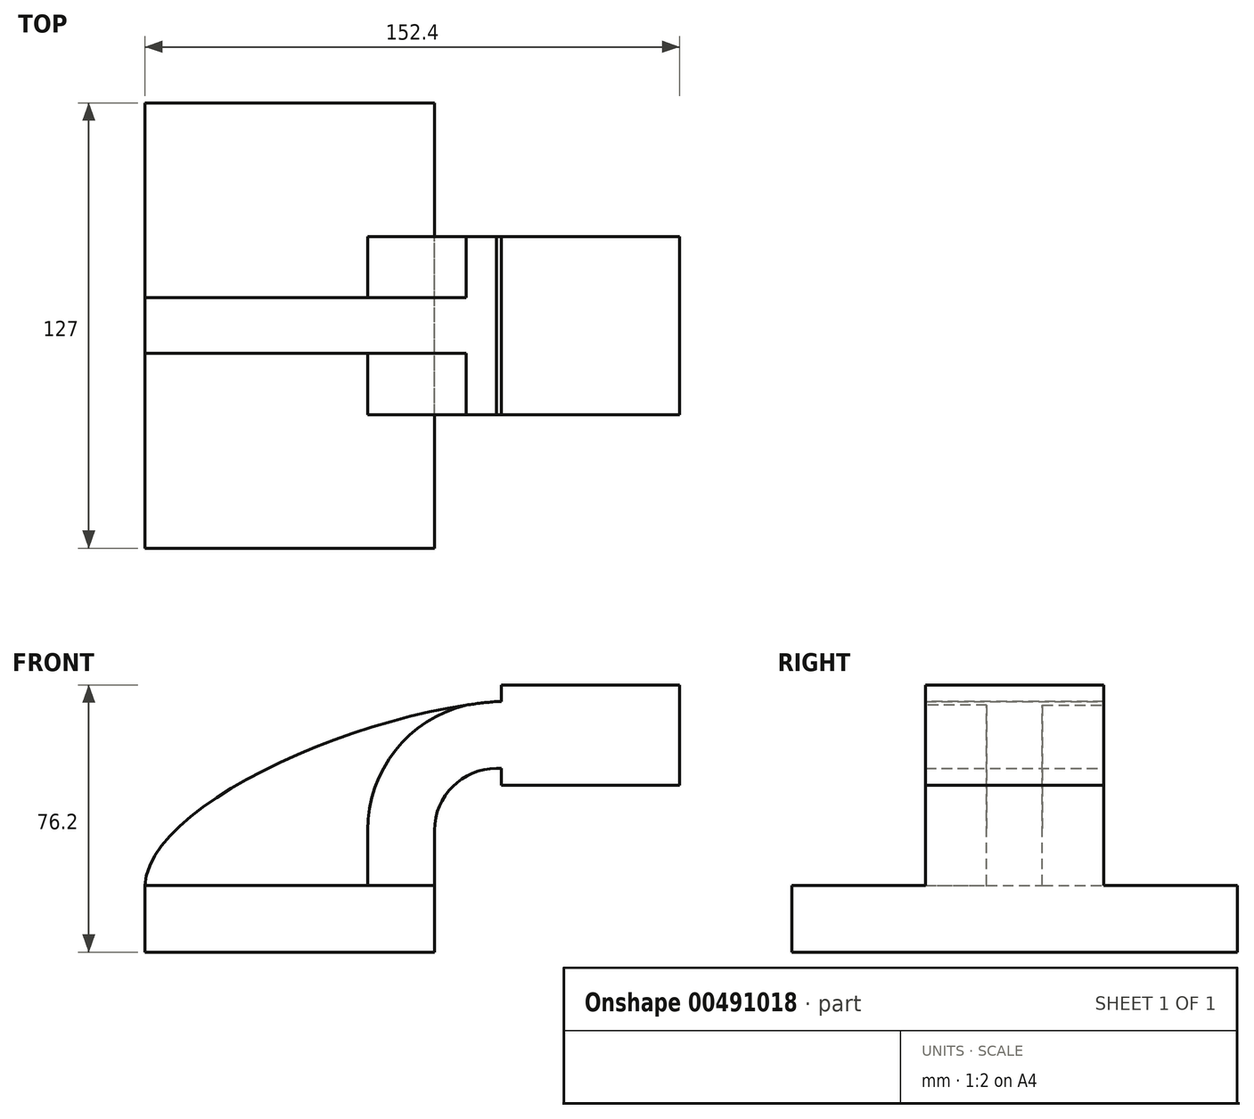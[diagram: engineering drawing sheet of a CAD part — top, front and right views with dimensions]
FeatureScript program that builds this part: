
annotation { "Feature Type Name" : "Feature", "Feature Type Description" : "" }
export const myFeature = defineFeature(function(context is Context, id is Id, definition is map)
    precondition{}
    {
        {
            var Q0;
            Q0=qCreatedBy(makeId("Front.planeOp"),FACE);
            var sketch = newSketch(context, id + "F0", { "sketchPlane" : qUnion([Q0])});
            skLineSegment(sketch, "E0.bottom", {"start": v(-41.28, 9.52) * mm, "end": v(41.27, 9.53) * mm});
            skLineSegment(sketch, "E0.top", {"start": v(-41.28, -9.52) * mm, "end": v(41.28, -9.52) * mm});
            skLineSegment(sketch, "E0.left", {"start": v(-41.28, 9.52) * mm, "end": v(-41.28, -9.53) * mm});
            skLineSegment(sketch, "E0.right", {"start": v(41.27, 9.53) * mm, "end": v(41.28, -9.52) * mm});
            skPoint(sketch, "E0.middle", {"position": v(0, 0) * mm});
            skLineSegment(sketch, "E1.bottom", {"start": v(60.32, 66.68) * mm, "end": v(111.12, 66.68) * mm});
            skLineSegment(sketch, "E1.top", {"start": v(60.32, 38.1) * mm, "end": v(111.12, 38.1) * mm});
            skLineSegment(sketch, "E1.left", {"start": v(60.32, 66.68) * mm, "end": v(60.32, 38.1) * mm});
            skLineSegment(sketch, "E1.right", {"start": v(111.12, 66.68) * mm, "end": v(111.12, 38.1) * mm});
            skPoint(sketch, "E1.middle", {"position": v(85.72, 52.39) * mm});
            skLineSegment(sketch, "E2", {"start": v(41.27, 9.53) * mm, "end": v(41.27, 25.25) * mm});
            skArc(sketch, "E3", {"start": v(41.27, 25.25) * mm, "mid": v(46.44, 37.71) * mm, "end": v(58.9, 42.88) * mm});
            skLineSegment(sketch, "E4", {"start": v(58.9, 42.88) * mm, "end": v(85.72, 42.88) * mm});
            skLineSegment(sketch, "E5.0", {"start": v(58.9, 61.93) * mm, "end": v(85.72, 61.93) * mm});
            skArc(sketch, "E5.1", {"start": v(22.22, 25.25) * mm, "mid": v(32.97, 51.18) * mm, "end": v(58.9, 61.93) * mm});
            skLineSegment(sketch, "E5.2", {"start": v(22.22, 9.53) * mm, "end": v(22.22, 25.25) * mm});
            skLineSegment(sketch, "E6", {"start": v(85.72, 38.1) * mm, "end": v(85.72, 66.68) * mm});
            skFitSpline(sketch, "E7", {"points": [v(-41.28, 9.53) * mm, v(58.9, 61.93) * mm], "startDerivative": vector(3.05, 68.36) * mm, "endDerivative": vector(121.34, 10.24) * mm});
            skSolve(sketch);
        }
        {
            var Q0;
            Q0=makeQuery(id+"F0.imprint","IMPRINT",FACE,{"disambiguationData":[TD([[makeQuery(id+"F0.imprint","IMPRINT",EDGE,{"derivedFrom":sQuery(id+"F0.wireOp",EDGE,"E0.top")}),1.0]])]});
            extrude(context, id + "F1", {"entities" : qUnion([Q0]), "endBound" : BoundingType.SYMMETRIC, "depth" : 127 * mm});
        }
        {
            var Q0;
            {var subQ1=sQuery(id+"F0.wireOp",EDGE,"E2");Q0=makeQuery(id+"F0.imprint","IMPRINT",FACE,{"disambiguationData":[TD([[makeQuery(id+"F0.imprint","IMPRINT",EDGE,{"derivedFrom":subQ1}),1.0]])]});}
            var Q1;
            {var subQ0=sQuery(id+"F0.wireOp",EDGE,"E5.0");var subQ1=sQuery(id+"F0.wireOp",EDGE,"E1.left");var subQ2=makeQuery(id+"F0.imprint","INTERSECT",VERTEX,{"derivedFrom":[subQ1,subQ0]});Q1=makeQuery(id+"F0.imprint","IMPRINT",FACE,{"disambiguationData":[TD([[makeQuery(id+"F0.imprint","IMPRINT",EDGE,{"disambiguationData":[TD([[subQ2,-1.0]])],"derivedFrom":subQ1}),1.0]])]});}
            var Q2;
            {var subQ0=sQuery(id+"F0.wireOp",EDGE,"E1.left");var subQ1=sQuery(id+"F0.wireOp",EDGE,"E1.top");var subQ2=makeQuery(id+"F0.imprint","INTERSECT",VERTEX,{"derivedFrom":[subQ1,subQ0]});Q2=makeQuery(id+"F0.imprint","IMPRINT",FACE,{"disambiguationData":[TD([[makeQuery(id+"F0.imprint","IMPRINT",EDGE,{"disambiguationData":[TD([[subQ2,-1.0]])],"derivedFrom":subQ1}),1.0]])]});}
            var Q3;
            {var subQ0=sQuery(id+"F0.wireOp",EDGE,"E1.left");var subQ1=sQuery(id+"F0.wireOp",EDGE,"E1.bottom");var subQ2=makeQuery(id+"F0.imprint","INTERSECT",VERTEX,{"derivedFrom":[subQ1,subQ0]});Q3=makeQuery(id+"F0.imprint","IMPRINT",FACE,{"disambiguationData":[TD([[makeQuery(id+"F0.imprint","IMPRINT",EDGE,{"disambiguationData":[TD([[subQ2,-1.0]])],"derivedFrom":subQ1}),-1.0]])]});}
            var Q4;
            {var subQ4=sQuery(id+"F0.wireOp",EDGE,"E1.right");Q4=makeQuery(id+"F0.imprint","IMPRINT",FACE,{"disambiguationData":[TD([[makeQuery(id+"F0.imprint","IMPRINT",EDGE,{"derivedFrom":subQ4}),-1.0]])]});}
            extrude(context, id + "F2", {"entities" : qUnion([Q0, Q1, Q2, Q3, Q4]), "operationType" : NewBodyOperationType.ADD, "endBound" : BoundingType.SYMMETRIC, "depth" : 50.8 * mm});
        }
        {
            var Q0;
            {var subQ3=sQuery(id+"F0.wireOp",EDGE,"E5.2");Q0=makeQuery(id+"F0.imprint","IMPRINT",FACE,{"disambiguationData":[TD([[makeQuery(id+"F0.imprint","IMPRINT",EDGE,{"derivedFrom":subQ3}),1.0]])]});}
            extrude(context, id + "F3", {"entities" : qUnion([Q0]), "operationType" : NewBodyOperationType.ADD, "endBound" : BoundingType.SYMMETRIC, "depth" : 15.88 * mm});
        }
    });
